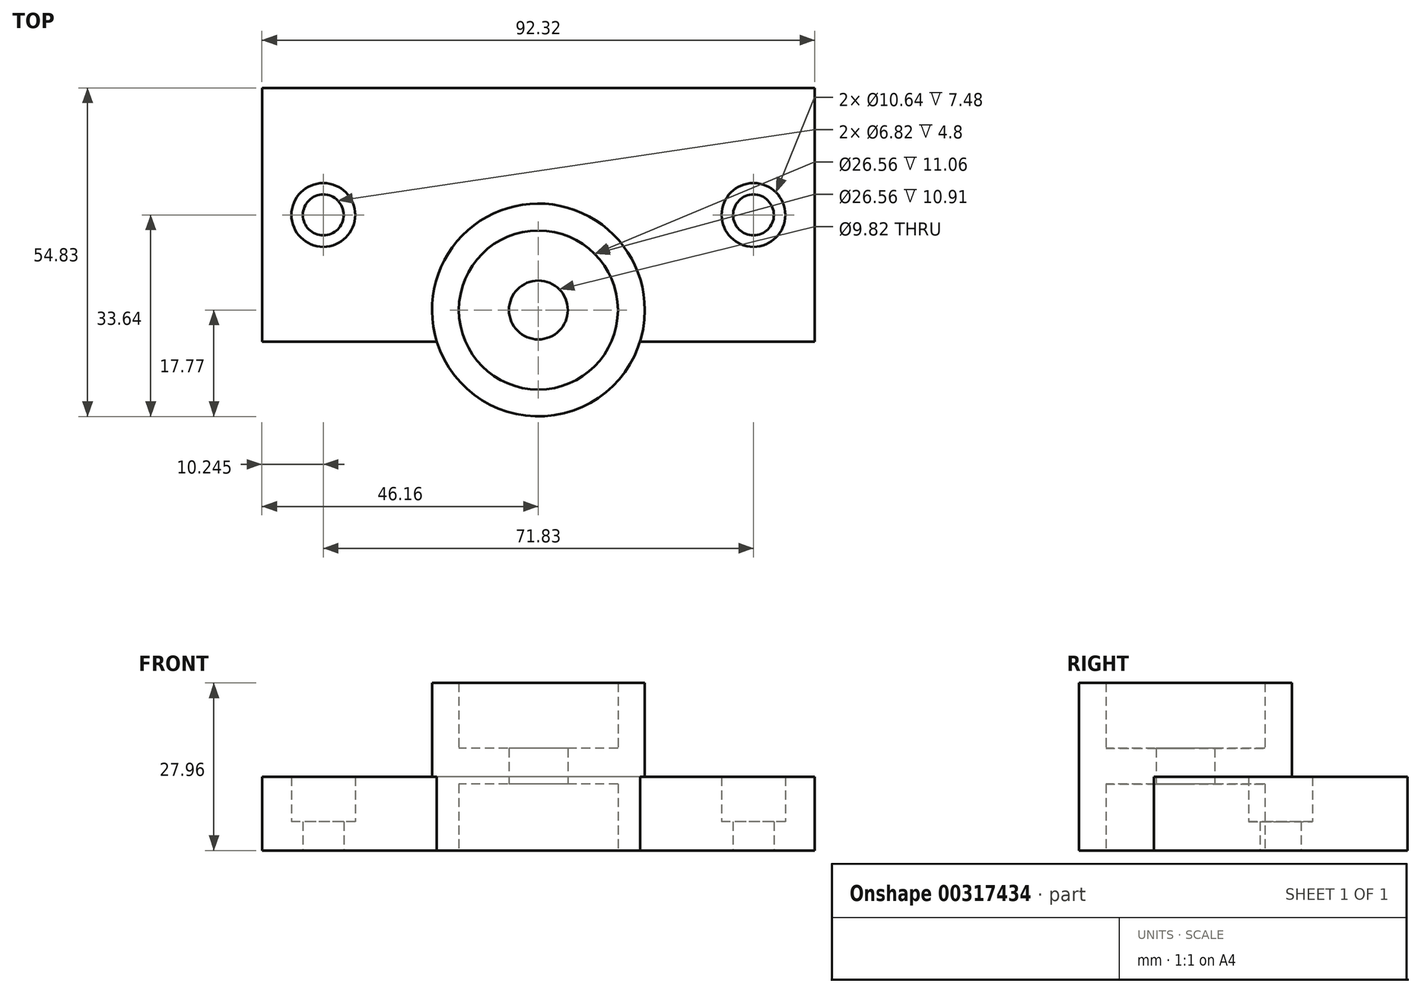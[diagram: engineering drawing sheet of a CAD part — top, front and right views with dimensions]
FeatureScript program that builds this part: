
annotation { "Feature Type Name" : "Feature", "Feature Type Description" : "" }
export const myFeature = defineFeature(function(context is Context, id is Id, definition is map)
    precondition{}
    {
        {
            var Q0;
            Q0=qCreatedBy(makeId("Top.planeOp"),FACE);
            var sketch = newSketch(context, id + "F0", { "sketchPlane" : qUnion([Q0])});
            skCircle(sketch, "E0", {"center": v(0, 0) * mm, "radius": 4.91 * mm});
            skCircle(sketch, "E1", {"center": v(0, 0) * mm, "radius": 13.28 * mm});
            skCircle(sketch, "E2", {"center": v(0, 0) * mm, "radius": 17.77 * mm});
            skSolve(sketch);
        }
        {
            var Q0;
            Q0=makeQuery(id+"F0.imprint","IMPRINT",FACE,{"disambiguationData":[TD([[makeQuery(id+"F0.imprint","IMPRINT",EDGE,{"derivedFrom":sQuery(id+"F0.wireOp",EDGE,"E1")}),-1.0]])]});
            var Q1;
            Q1=sQuery(id+"F0.wireOp",EDGE,"E2");
            var Q2;
            Q2=sQuery(id+"F0.wireOp",EDGE,"E1");
            extrude(context, id + "F1", {"entities" : qUnion([Q0]), "surfaceEntities" : qUnion([Q1, Q2]), "depth" : 27.96 * mm});
        }
        {
            var Q0;
            Q0=makeQuery(id+"F0.imprint","IMPRINT",FACE,{"disambiguationData":[TD([[makeQuery(id+"F0.imprint","IMPRINT",EDGE,{"derivedFrom":sQuery(id+"F0.wireOp",EDGE,"E0")}),-1.0]])]});
            extrude(context, id + "F2", {"entities" : qUnion([Q0]), "operationType" : NewBodyOperationType.ADD, "depth" : 17.05 * mm, "hasSecondDirection" : true, "secondDirectionOppositeDirection" : false, "secondDirectionDepth" : 11.06 * mm});
        }
        {
            var Q0;
            Q0=qCreatedBy(makeId("Top.planeOp"),FACE);
            var sketch = newSketch(context, id + "F3", { "sketchPlane" : qUnion([Q0])});
            skLineSegment(sketch, "E3.bottom", {"start": v(46.15, 37.06) * mm, "end": v(-46.16, 37.06) * mm});
            skLineSegment(sketch, "E3.top", {"start": v(46.16, -5.28) * mm, "end": v(-46.16, -5.28) * mm});
            skLineSegment(sketch, "E3.left", {"start": v(46.15, 37.06) * mm, "end": v(46.16, -5.28) * mm});
            skLineSegment(sketch, "E3.right", {"start": v(-46.16, 37.06) * mm, "end": v(-46.16, -5.28) * mm});
            skCircle(sketch, "E4", {"center": v(0, 0) * mm, "radius": 13.28 * mm});
            skCircle(sketch, "E5", {"center": v(-35.92, 15.87) * mm, "radius": 3.41 * mm});
            skCircle(sketch, "E6", {"center": v(35.91, 15.87) * mm, "radius": 3.41 * mm});
            skCircle(sketch, "E7", {"center": v(-35.92, 15.87) * mm, "radius": 5.32 * mm});
            skCircle(sketch, "E8", {"center": v(35.91, 15.87) * mm, "radius": 5.32 * mm});
            skSolve(sketch);
        }
        {
            var Q0;
            Q0=makeQuery(id+"F3.imprint","IMPRINT",FACE,{"disambiguationData":[TD([[makeQuery(id+"F3.imprint","IMPRINT",EDGE,{"derivedFrom":sQuery(id+"F3.wireOp",EDGE,"E3.bottom")}),1.0]])]});
            extrude(context, id + "F4", {"entities" : qUnion([Q0]), "operationType" : NewBodyOperationType.ADD, "depth" : 12.28 * mm});
        }
        {
            var Q0;
            Q0=makeQuery(id+"F3.imprint","IMPRINT",FACE,{"disambiguationData":[TD([[makeQuery(id+"F3.imprint","IMPRINT",EDGE,{"derivedFrom":sQuery(id+"F3.wireOp",EDGE,"E5")}),-1.0]])]});
            var Q1;
            Q1=makeQuery(id+"F3.imprint","IMPRINT",FACE,{"disambiguationData":[TD([[makeQuery(id+"F3.imprint","IMPRINT",EDGE,{"derivedFrom":sQuery(id+"F3.wireOp",EDGE,"E6")}),-1.0]])]});
            extrude(context, id + "F5", {"entities" : qUnion([Q0, Q1]), "operationType" : NewBodyOperationType.ADD, "depth" : 4.8 * mm});
        }
    });
